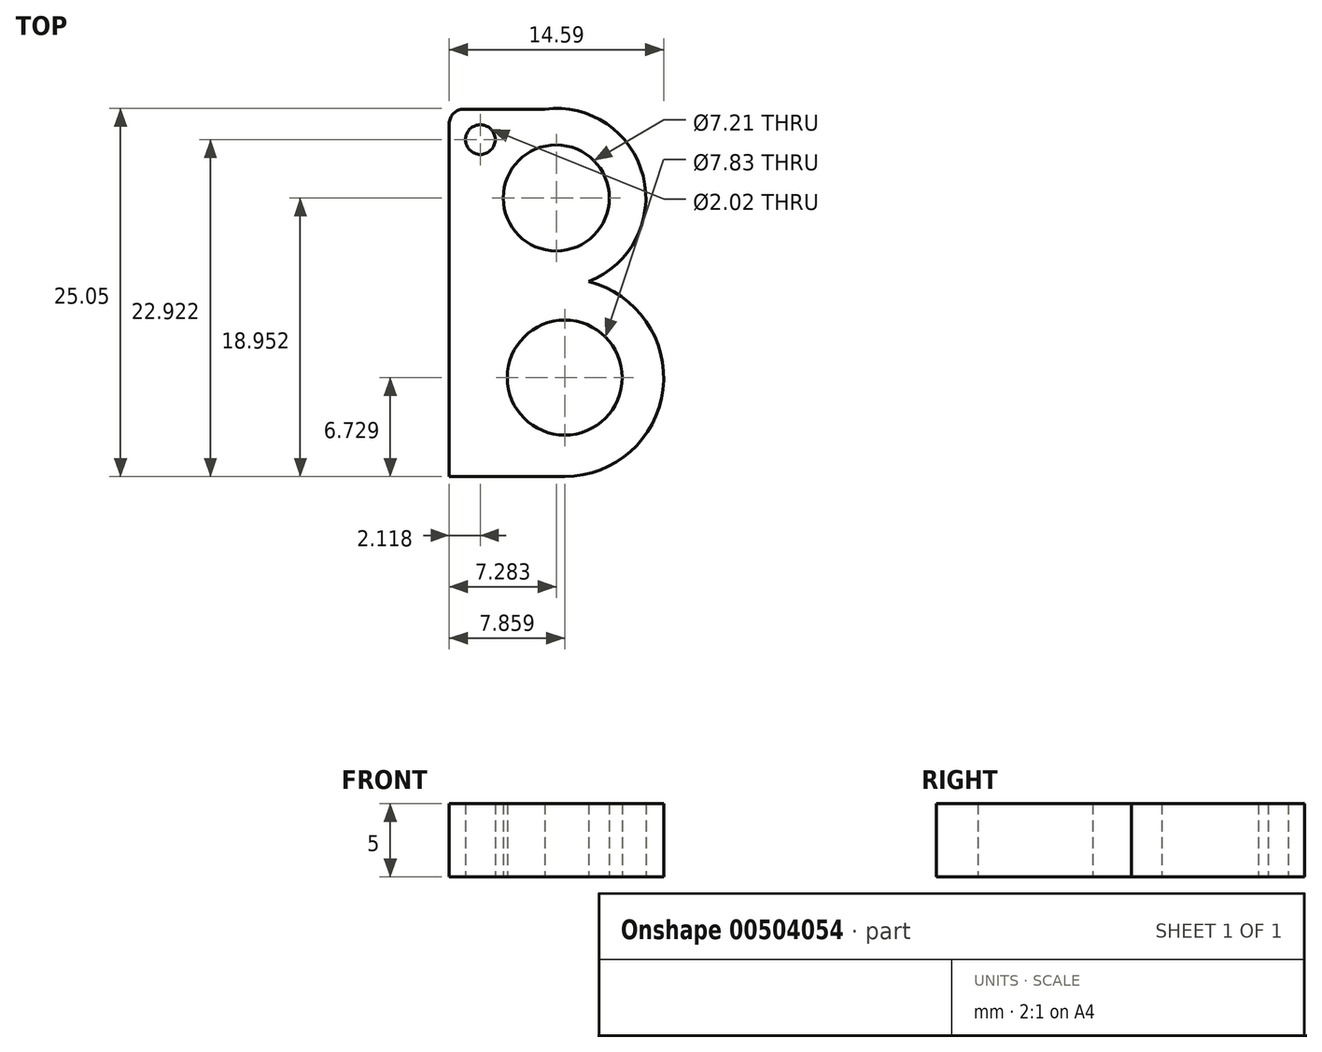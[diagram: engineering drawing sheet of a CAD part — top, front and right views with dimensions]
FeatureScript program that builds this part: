
annotation { "Feature Type Name" : "Feature", "Feature Type Description" : "" }
export const myFeature = defineFeature(function(context is Context, id is Id, definition is map)
    precondition{}
    {
        {
            var Q0;
            Q0=qCreatedBy(makeId("Top.planeOp"),FACE);
            var sketch = newSketch(context, id + "F0", { "sketchPlane" : qUnion([Q0])});
            skLineSegment(sketch, "E0", {"start": v(-24.63, 21.59) * mm, "end": v(-24.63, -2.41) * mm});
            skLineSegment(sketch, "E1", {"start": v(-24.63, -2.41) * mm, "end": v(-16.77, -2.41) * mm});
            skLineSegment(sketch, "E2", {"start": v(-23.63, 22.59) * mm, "end": v(-18.12, 22.59) * mm});
            skArc(sketch, "E3", {"start": v(-16.77, -2.41) * mm, "mid": v(-10.09, 3.5) * mm, "end": v(-15.16, 10.85) * mm});
            skArc(sketch, "E4", {"start": v(-15.16, 10.85) * mm, "mid": v(-11.44, 18.04) * mm, "end": v(-18.12, 22.59) * mm});
            skCircle(sketch, "E5", {"center": v(-17.35, 16.54) * mm, "radius": 3.6 * mm});
            skCircle(sketch, "E6", {"center": v(-16.77, 4.32) * mm, "radius": 3.91 * mm});
            skCircle(sketch, "E7", {"center": v(-22.51, 20.51) * mm, "radius": 1.01 * mm});
            skPoint(sketch, "E8.visualSharp", {"position": v(-24.63, 22.59) * mm});
            skArc(sketch, "E8.filletArc", {"start": v(-23.63, 22.59) * mm, "mid": v(-24.34, 22.3) * mm, "end": v(-24.63, 21.59) * mm});
            skSolve(sketch);
        }
        {
            var Q0;
            Q0 = qSketchRegion(id + "F0", true);
            extrude(context, id + "F1", {"entities" : qUnion([Q0]), "depth" : 5 * mm});
        }
    });
